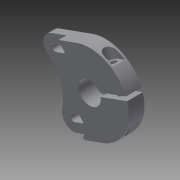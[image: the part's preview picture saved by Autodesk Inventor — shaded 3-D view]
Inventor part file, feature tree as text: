
AUTODESK INVENTOR PART (.ipt)
format: ipt  version: 2015 (Build 190159000, 159)  size: 210,944 bytes
history: native  units: in
note: dims shown in document units (in); Inventor stores cm internally (conversion verified against a paired STEP export)
features: sketch x5, extrude x4, projected_geometry x4, other x1, plane x1, mirror x1, fillet x1
ambient origin geometry x8: Origin, YZ Plane, XZ Plane, XY Plane, X Axis, Y Axis, Z Axis, Center Point
bodies: Solid1 (feature_tree)
feature tree (17):
  other  "mount_sketch.ipt"
  extrude  "Extrusion1"  Depth=0.5in TaperAngle=0.0deg
  extrude  "Extrusion2"  Depth=0.375in
  plane  "Work Plane1"
  mirror  "Mirror1"
  extrude  "Extrusion3"  Depth=0.5in TaperAngle=0.0deg
  extrude  "Extrusion4"  Depth=0.25in TaperAngle=0.0deg
  fillet  "Fillet1"  Radius=0.25in
  sketch  "Sketch2"  dims[d0=0.3937in d1=0.5in d2=0.0in]
  sketch  "Sketch3"  dims[d3=0.375in d4=0.8953in]
  sketch  "Sketch4"  dims[d5=0.4476in d6=0.5in d7=0.0in]
  projected_geometry  "Projected Loop1"
  projected_geometry  "Projected Loop2"
  sketch  "Sketch5"  dims[d8=0.201in d9=0.75in d10=0.0in d12=0.25in d13=0.0in]
  projected_geometry  "Projected Loop3"
  sketch  "Sketch6"  dims[d14=0.05in]
  projected_geometry  "Projected Loop4"
